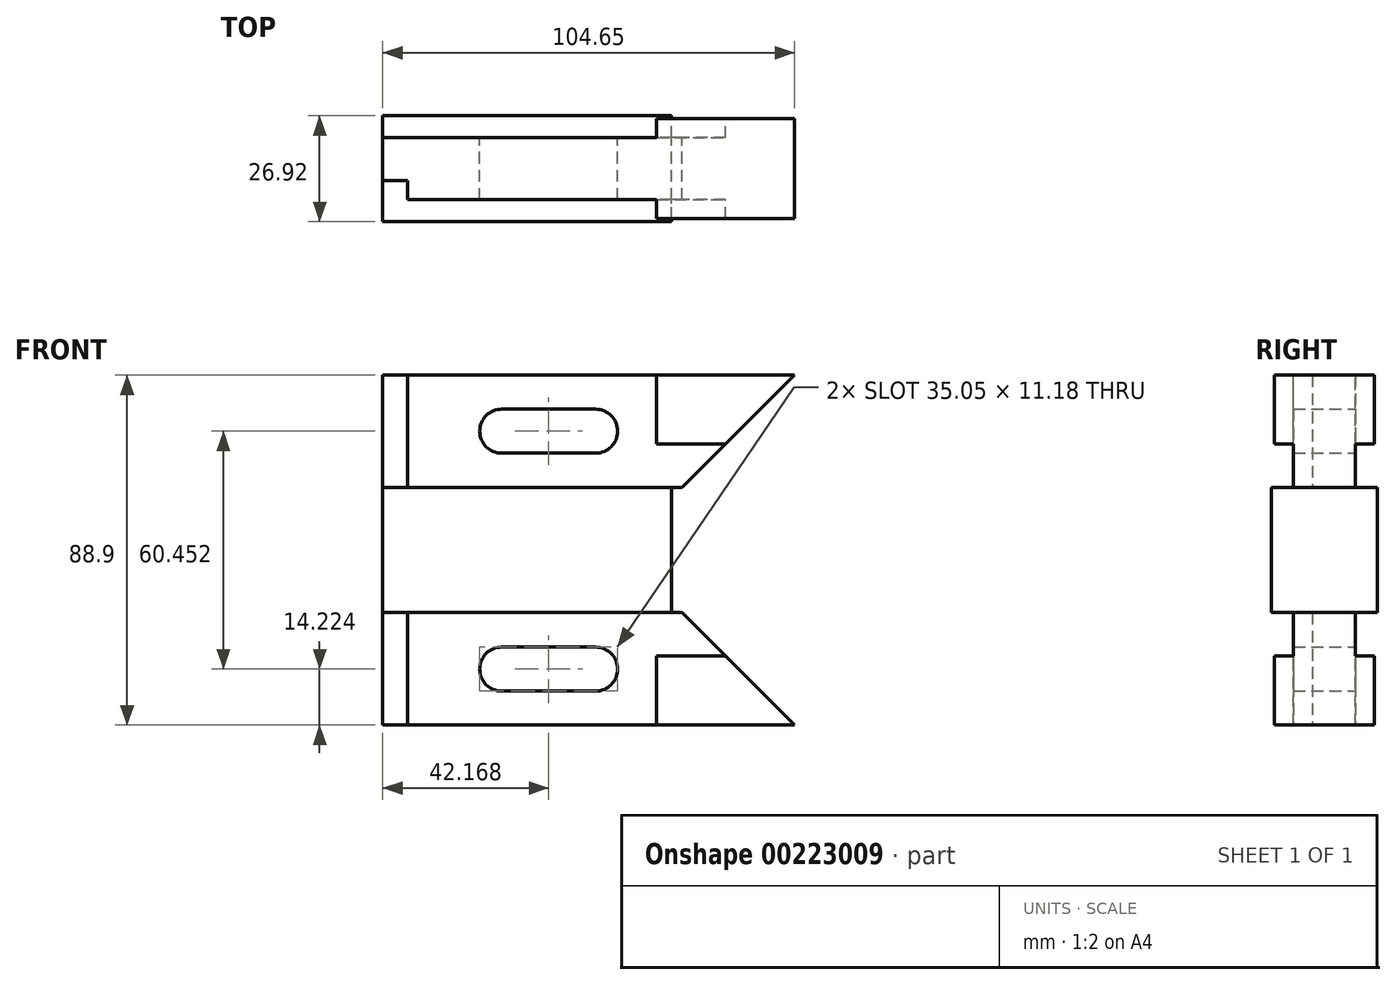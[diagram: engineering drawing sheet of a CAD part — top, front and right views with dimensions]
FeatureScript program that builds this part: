
annotation { "Feature Type Name" : "Feature", "Feature Type Description" : "" }
export const myFeature = defineFeature(function(context is Context, id is Id, definition is map)
    precondition{}
    {
        {
            var Q0;
            Q0=qCreatedBy(makeId("Front.planeOp"),FACE);
            var sketch = newSketch(context, id + "F0", { "sketchPlane" : qUnion([Q0])});
            skLineSegment(sketch, "E0", {"start": v(31.24, -44.45) * mm, "end": v(2.67, -15.87) * mm});
            skLineSegment(sketch, "E1", {"start": v(2.67, -15.87) * mm, "end": v(-73.4, -15.87) * mm});
            skLineSegment(sketch, "E2", {"start": v(-67.06, -15.87) * mm, "end": v(-67.06, -44.45) * mm});
            skLineSegment(sketch, "E3", {"start": v(-3.8, -44.45) * mm, "end": v(-3.8, -26.92) * mm});
            skLineSegment(sketch, "E4", {"start": v(-3.8, -26.92) * mm, "end": v(13.72, -26.92) * mm});
            skLineSegment(sketch, "E5", {"start": v(-43.18, -30.23) * mm, "end": v(-19.3, -30.23) * mm, "construction": true});
            skArc(sketch, "E6", {"start": v(-19.3, -35.81) * mm, "mid": v(-13.72, -30.23) * mm, "end": v(-19.3, -24.64) * mm});
            skArc(sketch, "E7", {"start": v(-43.18, -24.64) * mm, "mid": v(-48.77, -30.23) * mm, "end": v(-43.18, -35.81) * mm});
            skLineSegment(sketch, "E8", {"start": v(-43.18, -24.64) * mm, "end": v(-19.3, -24.64) * mm});
            skLineSegment(sketch, "E9", {"start": v(-43.18, -35.81) * mm, "end": v(-19.3, -35.81) * mm});
            skLineSegment(sketch, "E10", {"start": v(31.24, 44.45) * mm, "end": v(2.67, 15.87) * mm});
            skLineSegment(sketch, "E11", {"start": v(2.67, 15.87) * mm, "end": v(-73.4, 15.87) * mm});
            skLineSegment(sketch, "E12", {"start": v(13.72, 26.92) * mm, "end": v(-3.8, 26.92) * mm});
            skLineSegment(sketch, "E13", {"start": v(-3.8, 26.92) * mm, "end": v(-3.8, 44.45) * mm});
            skLineSegment(sketch, "E14", {"start": v(-67.06, 15.87) * mm, "end": v(-67.06, 44.45) * mm});
            skLineSegment(sketch, "E15", {"start": v(-43.18, 30.23) * mm, "end": v(-19.3, 30.23) * mm, "construction": true});
            skArc(sketch, "E16", {"start": v(-19.3, 24.64) * mm, "mid": v(-13.72, 30.23) * mm, "end": v(-19.3, 35.81) * mm});
            skArc(sketch, "E17", {"start": v(-43.18, 35.81) * mm, "mid": v(-48.77, 30.23) * mm, "end": v(-43.18, 24.64) * mm});
            skLineSegment(sketch, "E18", {"start": v(-43.18, 35.81) * mm, "end": v(-19.3, 35.81) * mm});
            skLineSegment(sketch, "E19", {"start": v(-43.18, 24.64) * mm, "end": v(-19.3, 24.64) * mm});
            skLineSegment(sketch, "E20", {"start": v(0, 15.87) * mm, "end": v(0, -15.87) * mm});
            skLineSegment(sketch, "E21", {"start": v(-73.4, 44.45) * mm, "end": v(-67.06, 44.45) * mm});
            skLineSegment(sketch, "E22", {"start": v(-67.06, 44.45) * mm, "end": v(-3.8, 44.45) * mm});
            skLineSegment(sketch, "E23", {"start": v(-3.8, 44.45) * mm, "end": v(31.24, 44.45) * mm});
            skLineSegment(sketch, "E24", {"start": v(-73.4, -44.45) * mm, "end": v(-67.06, -44.45) * mm});
            skLineSegment(sketch, "E25", {"start": v(31.24, -44.45) * mm, "end": v(-3.8, -44.45) * mm});
            skLineSegment(sketch, "E26", {"start": v(-3.8, -44.45) * mm, "end": v(-67.06, -44.45) * mm});
            skLineSegment(sketch, "E27", {"start": v(-43.18, -30.23) * mm, "end": v(-48.77, -30.23) * mm, "construction": true});
            skLineSegment(sketch, "E28", {"start": v(-19.3, -30.23) * mm, "end": v(-13.72, -30.23) * mm, "construction": true});
            skLineSegment(sketch, "E29", {"start": v(-43.18, 30.23) * mm, "end": v(-48.77, 30.23) * mm, "construction": true});
            skLineSegment(sketch, "E30", {"start": v(-19.3, 30.23) * mm, "end": v(-13.72, 30.23) * mm, "construction": true});
            skLineSegment(sketch, "E31", {"start": v(-48.77, 30.23) * mm, "end": v(-73.4, 30.23) * mm, "construction": true});
            skLineSegment(sketch, "E32", {"start": v(-48.77, -30.23) * mm, "end": v(-73.4, -30.23) * mm, "construction": true});
            skLineSegment(sketch, "E33", {"start": v(-73.4, 44.45) * mm, "end": v(-73.4, 15.87) * mm});
            skLineSegment(sketch, "E34", {"start": v(-73.4, 15.87) * mm, "end": v(-73.4, -15.87) * mm});
            skLineSegment(sketch, "E35", {"start": v(-73.4, -15.87) * mm, "end": v(-73.4, -44.45) * mm});
            skSolve(sketch);
        }
        {
            var Q0;
            {var subQ2=sQuery(id+"F0.wireOp",EDGE,"E20");Q0=makeQuery(id+"F0.imprint","IMPRINT",FACE,{"disambiguationData":[TD([[makeQuery(id+"F0.imprint","IMPRINT",EDGE,{"derivedFrom":subQ2}),-1.0]])]});}
            extrude(context, id + "F1", {"entities" : qUnion([Q0]), "endBound" : BoundingType.SYMMETRIC, "depth" : 26.92 * mm});
        }
        {
            var Q0;
            {var subQ5=sQuery(id+"F0.wireOp",EDGE,"E2");Q0=makeQuery(id+"F0.imprint","IMPRINT",FACE,{"disambiguationData":[TD([[makeQuery(id+"F0.imprint","IMPRINT",EDGE,{"derivedFrom":subQ5}),1.0]])]});}
            var Q1;
            {var subQ5=sQuery(id+"F0.wireOp",EDGE,"E12");Q1=makeQuery(id+"F0.imprint","IMPRINT",FACE,{"disambiguationData":[TD([[makeQuery(id+"F0.imprint","IMPRINT",EDGE,{"derivedFrom":subQ5}),1.0]])]});}
            extrude(context, id + "F2", {"entities" : qUnion([Q0, Q1]), "operationType" : NewBodyOperationType.ADD, "endBound" : BoundingType.SYMMETRIC, "depth" : 15.75 * mm});
        }
        {
            var Q0;
            {var subQ2=sQuery(id+"F0.wireOp",EDGE,"E12");Q0=makeQuery(id+"F0.imprint","IMPRINT",FACE,{"disambiguationData":[TD([[makeQuery(id+"F0.imprint","IMPRINT",EDGE,{"derivedFrom":subQ2}),-1.0]])]});}
            var Q1;
            Q1=makeQuery(id+"F0.imprint","IMPRINT",FACE,{"disambiguationData":[TD([[makeQuery(id+"F0.imprint","IMPRINT",EDGE,{"derivedFrom":sQuery(id+"F0.wireOp",EDGE,"E3")}),-1.0]])]});
            extrude(context, id + "F3", {"entities" : qUnion([Q0, Q1]), "operationType" : NewBodyOperationType.ADD, "endBound" : BoundingType.SYMMETRIC, "depth" : 25.4 * mm});
        }
        {
            var Q0;
            {var subQ2=sQuery(id+"F0.wireOp",EDGE,"E14");Q0=makeQuery(id+"F0.imprint","IMPRINT",FACE,{"disambiguationData":[TD([[makeQuery(id+"F0.imprint","IMPRINT",EDGE,{"derivedFrom":subQ2}),1.0]])]});}
            var Q1;
            {var subQ2=sQuery(id+"F0.wireOp",EDGE,"E2");Q1=makeQuery(id+"F0.imprint","IMPRINT",FACE,{"disambiguationData":[TD([[makeQuery(id+"F0.imprint","IMPRINT",EDGE,{"derivedFrom":subQ2}),-1.0]])]});}
            extrude(context, id + "F4", {"entities" : qUnion([Q0, Q1]), "operationType" : NewBodyOperationType.ADD, "endBound" : BoundingType.SYMMETRIC, "depth" : 15.75 * mm});
        }
        {
            var Q0;
            {var subQ0=sQuery(id+"F0.wireOp",EDGE,"E14");var subQ1=sQuery(id+"F0.wireOp",EDGE,"E11");Q0=makeQuery(id+"F4.boolean.opBoolean","MERGE",FACE,{"derivedFrom":[makeQuery(id+"F2.opExtrude","CAP_FACE",FACE,{"disambiguationData":[OSD([sQuery(id+"F0.wireOp",EDGE,"E10"),subQ1,sQuery(id+"F0.wireOp",EDGE,"E12"),sQuery(id+"F0.wireOp",EDGE,"E13"),subQ0,sQuery(id+"F0.wireOp",EDGE,"E16"),sQuery(id+"F0.wireOp",EDGE,"E17"),sQuery(id+"F0.wireOp",EDGE,"E18"),sQuery(id+"F0.wireOp",EDGE,"E19"),sQuery(id+"F0.wireOp",EDGE,"E22")])],"isStart":false}),makeQuery(id+"F4.opExtrude","CAP_FACE",FACE,{"disambiguationData":[OSD([subQ1,subQ0,sQuery(id+"F0.wireOp",EDGE,"E21"),sQuery(id+"F0.wireOp",EDGE,"E33")])],"isStart":false})]});}
            var sketch = newSketch(context, id + "F5", { "sketchPlane" : qUnion([Q0])});
            skLineSegment(sketch, "E36.0", {"start": v(-67.06, 15.87) * mm, "end": v(-67.06, 44.45) * mm});
            skPoint(sketch, "E37.0", {"position": v(-70.23, 44.45) * mm});
            skLineSegment(sketch, "E38.0", {"start": v(-73.4, 44.45) * mm, "end": v(-73.4, 15.87) * mm});
            skLineSegment(sketch, "E39.0", {"start": v(-73.4, 44.45) * mm, "end": v(-67.06, 44.45) * mm});
            skLineSegment(sketch, "E40.0", {"start": v(2.67, 15.87) * mm, "end": v(-73.4, 15.87) * mm});
            skLineSegment(sketch, "E41.0", {"start": v(2.67, -15.87) * mm, "end": v(-73.4, -15.87) * mm});
            skLineSegment(sketch, "E42.0", {"start": v(-73.4, -15.87) * mm, "end": v(-73.4, -44.45) * mm});
            skLineSegment(sketch, "E43.0", {"start": v(-67.06, -15.87) * mm, "end": v(-67.06, -44.45) * mm});
            skLineSegment(sketch, "E44.0", {"start": v(-73.4, -44.45) * mm, "end": v(-67.06, -44.45) * mm});
            skSolve(sketch);
        }
        {
            var Q0;
            Q0 = qSketchRegion(id + "F5", true);
            extrude(context, id + "F6", {"entities" : qUnion([Q0]), "operationType" : NewBodyOperationType.REMOVE, "oppositeDirection" : true, "depth" : 4.83 * mm});
        }
    });
